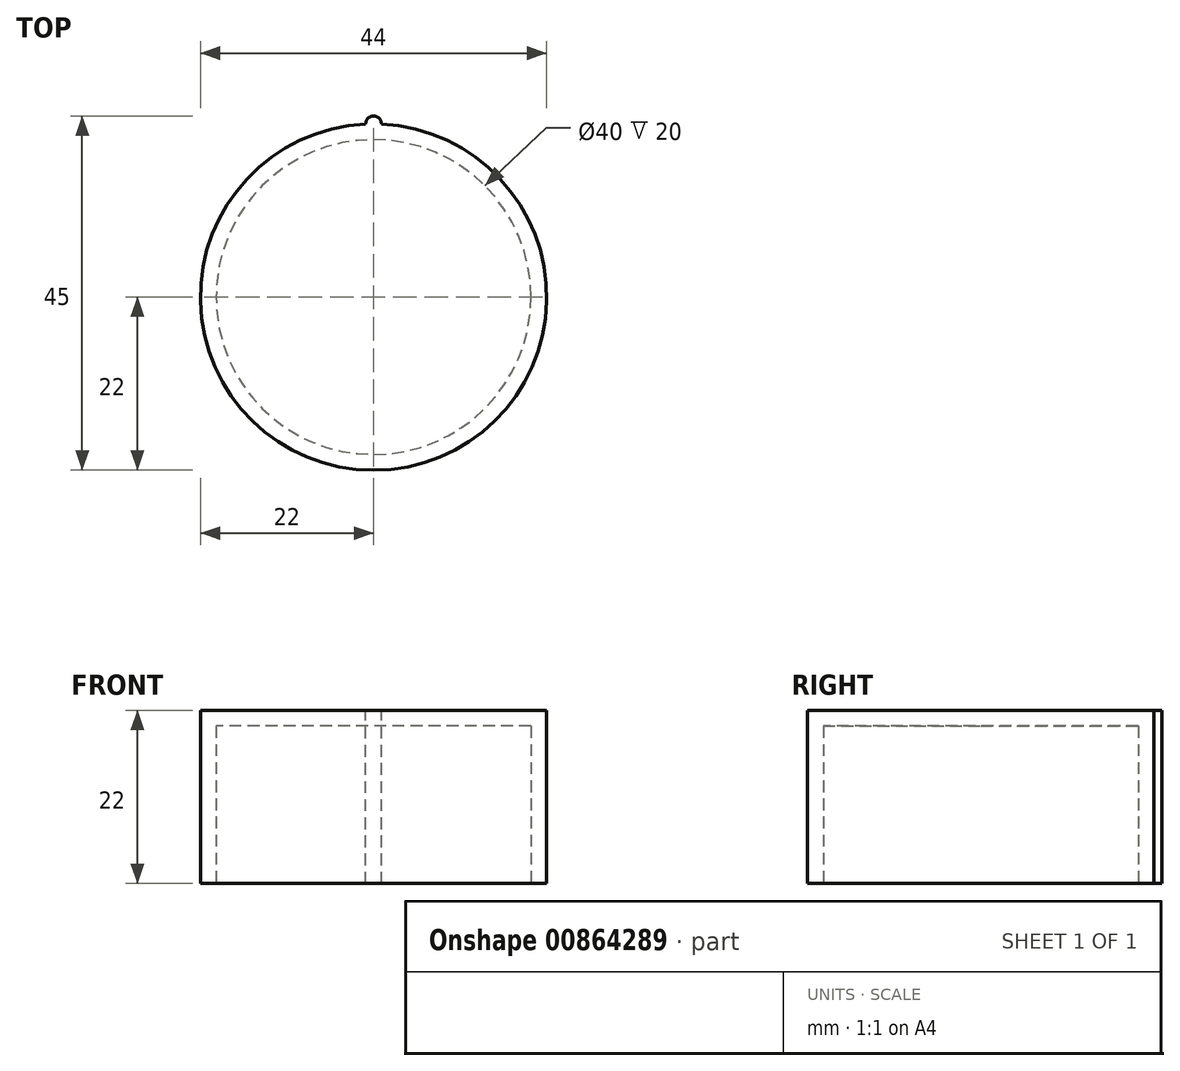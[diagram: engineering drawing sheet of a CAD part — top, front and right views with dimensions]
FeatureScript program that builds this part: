
annotation { "Feature Type Name" : "Feature", "Feature Type Description" : "" }
export const myFeature = defineFeature(function(context is Context, id is Id, definition is map)
    precondition{}
    {
        {
            var Q0;
            Q0=qCreatedBy(makeId("Top.planeOp"),FACE);
            var sketch = newSketch(context, id + "F0", { "sketchPlane" : qUnion([Q0])});
            skCircle(sketch, "E0", {"center": v(0, 0) * mm, "radius": 20 * mm});
            skSolve(sketch);
        }
        {
            var Q0;
            Q0=makeQuery(id+"F0.imprint","IMPRINT",FACE,{"disambiguationData":[TD([[makeQuery(id+"F0.imprint","IMPRINT",EDGE,{"derivedFrom":sQuery(id+"F0.wireOp",EDGE,"E0")}),1.0]])]});
            extrude(context, id + "F1", {"entities" : qUnion([Q0]), "depth" : 20 * mm, "offsetDistance" : 25 * mm});
        }
        {
            var Q0;
            Q0=makeQuery(id+"F1.opExtrude","CAP_FACE",FACE,{"disambiguationData":[OSD([sQuery(id+"F0.wireOp",EDGE,"E0")])],"isStart":true});
            shell(context, id + "F2", {"entities" : qUnion([Q0]), "thickness" : 2 * mm, "oppositeDirection" : true});
        }
        {
            var Q0;
            Q0=makeQuery(id+"F1.opExtrude","CAP_FACE",FACE,{"disambiguationData":[OSD([sQuery(id+"F0.wireOp",EDGE,"E0")])],"isStart":false});
            var sketch = newSketch(context, id + "F3", { "sketchPlane" : qUnion([Q0])});
            skCircle(sketch, "E1", {"center": v(0, 0) * mm, "radius": 22 * mm});
            skArc(sketch, "E2", {"start": v(1, 21.98) * mm, "mid": v(0, 23) * mm, "end": v(-1, 21.98) * mm});
            skSolve(sketch);
        }
        {
            var Q0;
            {var subQ0=sQuery(id+"F3.wireOp",EDGE,"E2");Q0=makeQuery(id+"F3.imprint","IMPRINT",FACE,{"disambiguationData":[TD([[makeQuery(id+"F3.imprint","IMPRINT",EDGE,{"derivedFrom":subQ0}),1.0]])]});}
            var Q1;
            Q1=makeQuery(id+"F1.opExtrude","CAP_FACE",FACE,{"disambiguationData":[OSD([sQuery(id+"F0.wireOp",EDGE,"E0")])],"isStart":true});
            extrude(context, id + "F4", {"entities" : qUnion([Q0]), "operationType" : NewBodyOperationType.ADD, "endBound" : BoundingType.UP_TO_SURFACE, "oppositeDirection" : true, "depth" : 25 * mm, "endBoundEntityFace" : qUnion([Q1]), "offsetDistance" : 25 * mm});
        }
    });
